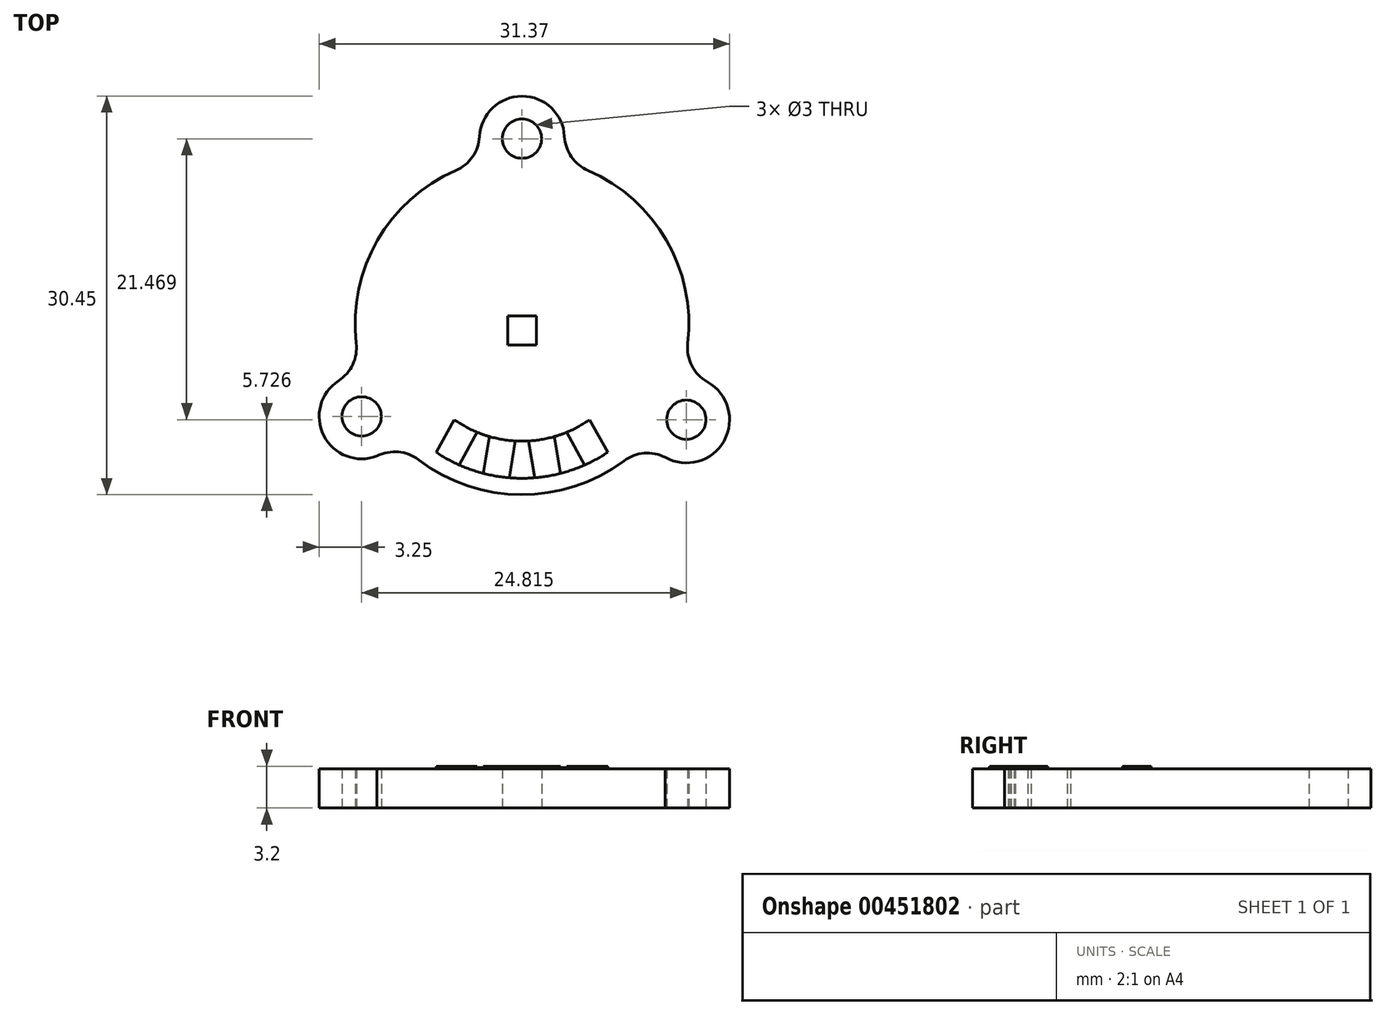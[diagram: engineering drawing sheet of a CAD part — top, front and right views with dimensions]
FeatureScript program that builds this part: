
annotation { "Feature Type Name" : "Feature", "Feature Type Description" : "" }
export const myFeature = defineFeature(function(context is Context, id is Id, definition is map)
    precondition{}
    {
        {
            var Q0;
            Q0=qCreatedBy(makeId("Top.planeOp"),FACE);
            var sketch = newSketch(context, id + "F0", { "sketchPlane" : qUnion([Q0])});
            skPoint(sketch, "E0.0.midPoint", {"position": v(6.28, 3.41) * mm});
            skArc(sketch, "E1", {"start": v(3.25, 14.31) * mm, "mid": v(0, 17.4) * mm, "end": v(-3.25, 14.31) * mm});
            skArc(sketch, "E2", {"start": v(-14.02, -4.35) * mm, "mid": v(-15.15, -8.55) * mm, "end": v(-11.08, -10.1) * mm});
            skArc(sketch, "E3", {"start": v(10.95, -10.2) * mm, "mid": v(15.44, -8.94) * mm, "end": v(14.18, -4.44) * mm});
            skPoint(sketch, "E4.visualSharp", {"position": v(-2.77, 12.45) * mm});
            skArc(sketch, "E4.filletArc", {"start": v(-5.05, 11.71) * mm, "mid": v(-3.78, 12.75) * mm, "end": v(-3.25, 14.31) * mm});
            skPoint(sketch, "E5.visualSharp", {"position": v(2.77, 12.45) * mm});
            skArc(sketch, "E5.filletArc", {"start": v(3.25, 14.31) * mm, "mid": v(3.78, 12.75) * mm, "end": v(5.05, 11.71) * mm});
            skPoint(sketch, "E6.visualSharp", {"position": v(12.1, -4.06) * mm});
            skArc(sketch, "E6.filletArc", {"start": v(12.67, -1.48) * mm, "mid": v(12.98, -3.2) * mm, "end": v(14.18, -4.44) * mm});
            skPoint(sketch, "E7.visualSharp", {"position": v(-12.17, -3.82) * mm});
            skArc(sketch, "E7.filletArc", {"start": v(-14.02, -4.35) * mm, "mid": v(-12.93, -3.1) * mm, "end": v(-12.67, -1.48) * mm});
            skCircle(sketch, "E8", {"center": v(0, 14.15) * mm, "radius": 1.5 * mm});
            skCircle(sketch, "E9", {"center": v(-12.25, -7.07) * mm, "radius": 1.5 * mm});
            skCircle(sketch, "E10", {"center": v(12.56, -7.32) * mm, "radius": 1.5 * mm});
            skArc(sketch, "E11", {"start": v(12.67, -1.48) * mm, "mid": v(11.05, 6.38) * mm, "end": v(5.05, 11.71) * mm});
            skArc(sketch, "E12.trimOffspring", {"start": v(-5.05, 11.71) * mm, "mid": v(-11.05, 6.38) * mm, "end": v(-12.67, -1.48) * mm});
            skPoint(sketch, "E13.0.midPoint", {"position": v(0, -7.07) * mm});
            skPoint(sketch, "E14.visualSharp", {"position": v(12.45, -3.91) * mm});
            skArc(sketch, "E14.filletArc", {"start": v(12.67, -1.48) * mm, "mid": v(12.93, -3.1) * mm, "end": v(14.02, -4.35) * mm});
            skPoint(sketch, "E15.visualSharp", {"position": v(9.61, -8.83) * mm});
            skArc(sketch, "E15.filletArc", {"start": v(10.95, -10.2) * mm, "mid": v(9.33, -9.89) * mm, "end": v(7.8, -10.47) * mm});
            skPoint(sketch, "E16.visualSharp", {"position": v(-9.61, -8.83) * mm});
            skArc(sketch, "E16.filletArc", {"start": v(-7.9, -10.39) * mm, "mid": v(-9.45, -9.79) * mm, "end": v(-11.08, -10.1) * mm});
            skArc(sketch, "E17", {"start": v(-7.9, -10.39) * mm, "mid": v(-0.07, -13.05) * mm, "end": v(7.8, -10.47) * mm});
            skSolve(sketch);
        }
        {
            var Q0;
            Q0=qSketchRegion(id+"F0",true);
            extrude(context, id + "F1", {"entities" : qUnion([Q0]), "depth" : 3 * mm, "offsetDistance" : 25 * mm});
        }
        {
            var Q0;
            Q0=makeQuery(id+"F1.opExtrude","CAP_FACE",FACE,{"disambiguationData":[OSD([sQuery(id+"F0.wireOp",EDGE,"C7QRfPFi-vLwI-X6gj-dWor-JbQLZ58fUFdR"),sQuery(id+"F0.wireOp",EDGE,"yMvEykNg-osCq-zqkn-151P-fJv8dIBG2HYN"),sQuery(id+"F0.wireOp",EDGE,"E1"),sQuery(id+"F0.wireOp",EDGE,"E2"),sQuery(id+"F0.wireOp",EDGE,"E3"),sQuery(id+"F0.wireOp",EDGE,"e72fb2e6-fbc5-47df-a29e-faecbfe39cbd.trimOffspring"),sQuery(id+"F0.wireOp",EDGE,"VexWzNiS-FvnS-RJBV-kCyA-mg64O8heLdvj"),sQuery(id+"F0.wireOp",EDGE,"41f6cdd4-8975-404a-b7e2-70d8f0a7ac2c.trimOffspring"),sQuery(id+"F0.wireOp",EDGE,"E4.filletArc"),sQuery(id+"F0.wireOp",EDGE,"E5.filletArc"),sQuery(id+"F0.wireOp",EDGE,"E6.filletArc"),sQuery(id+"F0.wireOp",EDGE,"E7.filletArc"),sQuery(id+"F0.wireOp",EDGE,"E8"),sQuery(id+"F0.wireOp",EDGE,"E9"),sQuery(id+"F0.wireOp",EDGE,"E10")])],"isStart":false});
            var sketch = newSketch(context, id + "F2", { "sketchPlane" : qUnion([Q0])});
            skPoint(sketch, "E18", {"position": v(0, -0.5) * mm});
            skPoint(sketch, "E18.positionSnap0", {"position": v(0, -10.1) * mm});
            skLineSegment(sketch, "E19.bottom", {"start": v(1.1, 0.6) * mm, "end": v(-1.1, 0.6) * mm});
            skLineSegment(sketch, "E19.top", {"start": v(1.1, -1.6) * mm, "end": v(-1.1, -1.6) * mm});
            skLineSegment(sketch, "E19.left", {"start": v(1.1, 0.6) * mm, "end": v(1.1, -1.6) * mm});
            skLineSegment(sketch, "E19.right", {"start": v(-1.1, 0.6) * mm, "end": v(-1.1, -1.6) * mm});
            skSolve(sketch);
        }
        {
            var Q0;
            Q0=qSketchRegion(id+"F2",true);
            extrude(context, id + "F3", {"entities" : qUnion([Q0]), "operationType" : NewBodyOperationType.ADD, "depth" : 0.2 * mm, "offsetDistance" : 25 * mm});
        }
        {
            var Q0;
            Q0=makeQuery(id+"F1.opExtrude","CAP_FACE",FACE,{"disambiguationData":[OSD([sQuery(id+"F0.wireOp",EDGE,"C7QRfPFi-vLwI-X6gj-dWor-JbQLZ58fUFdR"),sQuery(id+"F0.wireOp",EDGE,"yMvEykNg-osCq-zqkn-151P-fJv8dIBG2HYN"),sQuery(id+"F0.wireOp",EDGE,"E1"),sQuery(id+"F0.wireOp",EDGE,"E2"),sQuery(id+"F0.wireOp",EDGE,"E3"),sQuery(id+"F0.wireOp",EDGE,"e72fb2e6-fbc5-47df-a29e-faecbfe39cbd.trimOffspring"),sQuery(id+"F0.wireOp",EDGE,"VexWzNiS-FvnS-RJBV-kCyA-mg64O8heLdvj"),sQuery(id+"F0.wireOp",EDGE,"41f6cdd4-8975-404a-b7e2-70d8f0a7ac2c.trimOffspring"),sQuery(id+"F0.wireOp",EDGE,"E4.filletArc"),sQuery(id+"F0.wireOp",EDGE,"E5.filletArc"),sQuery(id+"F0.wireOp",EDGE,"E6.filletArc"),sQuery(id+"F0.wireOp",EDGE,"E7.filletArc"),sQuery(id+"F0.wireOp",EDGE,"E8"),sQuery(id+"F0.wireOp",EDGE,"E9"),sQuery(id+"F0.wireOp",EDGE,"E10")])],"isStart":false});
            var sketch = newSketch(context, id + "F4", { "sketchPlane" : qUnion([Q0])});
            skPoint(sketch, "E20.middle.positionSnap0", {"position": v(0, -1.6) * mm});
            skPoint(sketch, "E20.centerSnap0", {"position": v(0, -1.6) * mm});
            skPoint(sketch, "E21", {"position": v(0, 0) * mm});
            skPoint(sketch, "E21.positionSnap0", {"position": v(-1.1, -0.5) * mm});
            skLineSegment(sketch, "E22.left", {"start": v(-2.47, -8.62) * mm, "end": v(-2.95, -11.43) * mm});
            skLineSegment(sketch, "E22.right", {"start": v(-0.5, -8.95) * mm, "end": v(-0.98, -11.76) * mm});
            skPoint(sketch, "E23", {"position": v(-0.5, -8.95) * mm});
            skPoint(sketch, "E24", {"position": v(0.5, -8.95) * mm});
            skPoint(sketch, "E25", {"position": v(3.42, -8.29) * mm});
            skPoint(sketch, "E26", {"position": v(-3.42, -8.29) * mm});
            skLineSegment(sketch, "E27.left", {"start": v(-5.18, -7.32) * mm, "end": v(-6.55, -9.82) * mm});
            skLineSegment(sketch, "E27.right", {"start": v(-3.42, -8.29) * mm, "end": v(-4.8, -10.78) * mm});
            skLineSegment(sketch, "E28.left", {"start": v(0.5, -8.95) * mm, "end": v(0.98, -11.76) * mm});
            skLineSegment(sketch, "E28.right", {"start": v(2.47, -8.62) * mm, "end": v(2.95, -11.43) * mm});
            skPoint(sketch, "E29", {"position": v(2.47, -8.62) * mm});
            skLineSegment(sketch, "E30.left", {"start": v(3.42, -8.29) * mm, "end": v(4.8, -10.78) * mm});
            skLineSegment(sketch, "E30.right", {"start": v(5.18, -7.32) * mm, "end": v(6.55, -9.82) * mm});
            skPoint(sketch, "E31", {"position": v(5.18, -7.32) * mm});
            skArc(sketch, "E32", {"start": v(-5.18, -7.32) * mm, "mid": v(0, -8.97) * mm, "end": v(5.18, -7.32) * mm});
            skArc(sketch, "E33", {"start": v(-6.55, -9.82) * mm, "mid": v(0, -11.8) * mm, "end": v(6.55, -9.82) * mm});
            skSolve(sketch);
        }
        {
            var Q0;
            {var subQ0=sQuery(id+"F4.wireOp",EDGE,"E27.left");Q0=makeQuery(id+"F4.imprint","IMPRINT",FACE,{"disambiguationData":[TD([[makeQuery(id+"F4.imprint","IMPRINT",EDGE,{"derivedFrom":subQ0}),1.0]])]});}
            var Q1;
            {var subQ0=sQuery(id+"F4.wireOp",EDGE,"E22.left");Q1=makeQuery(id+"F4.imprint","IMPRINT",FACE,{"disambiguationData":[TD([[makeQuery(id+"F4.imprint","IMPRINT",EDGE,{"derivedFrom":subQ0}),-1.0]])]});}
            var Q2;
            {var subQ0=sQuery(id+"F4.wireOp",EDGE,"E22.left");Q2=makeQuery(id+"F4.imprint","IMPRINT",FACE,{"disambiguationData":[TD([[makeQuery(id+"F4.imprint","IMPRINT",EDGE,{"derivedFrom":subQ0}),1.0]])]});}
            var Q3;
            {var subQ0=sQuery(id+"F4.wireOp",EDGE,"E22.right");Q3=makeQuery(id+"F4.imprint","IMPRINT",FACE,{"disambiguationData":[TD([[makeQuery(id+"F4.imprint","IMPRINT",EDGE,{"derivedFrom":subQ0}),1.0]])]});}
            var Q4;
            {var subQ0=sQuery(id+"F4.wireOp",EDGE,"E28.left");Q4=makeQuery(id+"F4.imprint","IMPRINT",FACE,{"disambiguationData":[TD([[makeQuery(id+"F4.imprint","IMPRINT",EDGE,{"derivedFrom":subQ0}),1.0]])]});}
            var Q5;
            {var subQ0=sQuery(id+"F4.wireOp",EDGE,"E28.right");Q5=makeQuery(id+"F4.imprint","IMPRINT",FACE,{"disambiguationData":[TD([[makeQuery(id+"F4.imprint","IMPRINT",EDGE,{"derivedFrom":subQ0}),1.0]])]});}
            var Q6;
            {var subQ0=sQuery(id+"F4.wireOp",EDGE,"E30.left");Q6=makeQuery(id+"F4.imprint","IMPRINT",FACE,{"disambiguationData":[TD([[makeQuery(id+"F4.imprint","IMPRINT",EDGE,{"derivedFrom":subQ0}),1.0]])]});}
            extrude(context, id + "F5", {"entities" : qUnion([Q0, Q1, Q2, Q3, Q4, Q5, Q6]), "operationType" : NewBodyOperationType.ADD, "depth" : 0.1 * mm, "offsetDistance" : 25 * mm});
        }
        {
            var Q0;
            {var subQ0=sQuery(id+"F4.wireOp",EDGE,"E27.left");Q0=makeQuery(id+"F4.imprint","IMPRINT",FACE,{"disambiguationData":[TD([[makeQuery(id+"F4.imprint","IMPRINT",EDGE,{"derivedFrom":subQ0}),1.0]])]});}
            var Q1;
            {var subQ0=sQuery(id+"F4.wireOp",EDGE,"E22.left");Q1=makeQuery(id+"F4.imprint","IMPRINT",FACE,{"disambiguationData":[TD([[makeQuery(id+"F4.imprint","IMPRINT",EDGE,{"derivedFrom":subQ0}),1.0]])]});}
            var Q2;
            {var subQ0=sQuery(id+"F4.wireOp",EDGE,"E28.left");Q2=makeQuery(id+"F4.imprint","IMPRINT",FACE,{"disambiguationData":[TD([[makeQuery(id+"F4.imprint","IMPRINT",EDGE,{"derivedFrom":subQ0}),1.0]])]});}
            var Q3;
            {var subQ0=sQuery(id+"F4.wireOp",EDGE,"E30.left");Q3=makeQuery(id+"F4.imprint","IMPRINT",FACE,{"disambiguationData":[TD([[makeQuery(id+"F4.imprint","IMPRINT",EDGE,{"derivedFrom":subQ0}),1.0]])]});}
            extrude(context, id + "F6", {"entities" : qUnion([Q0, Q1, Q2, Q3]), "operationType" : NewBodyOperationType.ADD, "depth" : 0.2 * mm, "offsetDistance" : 25 * mm});
        }
    });
